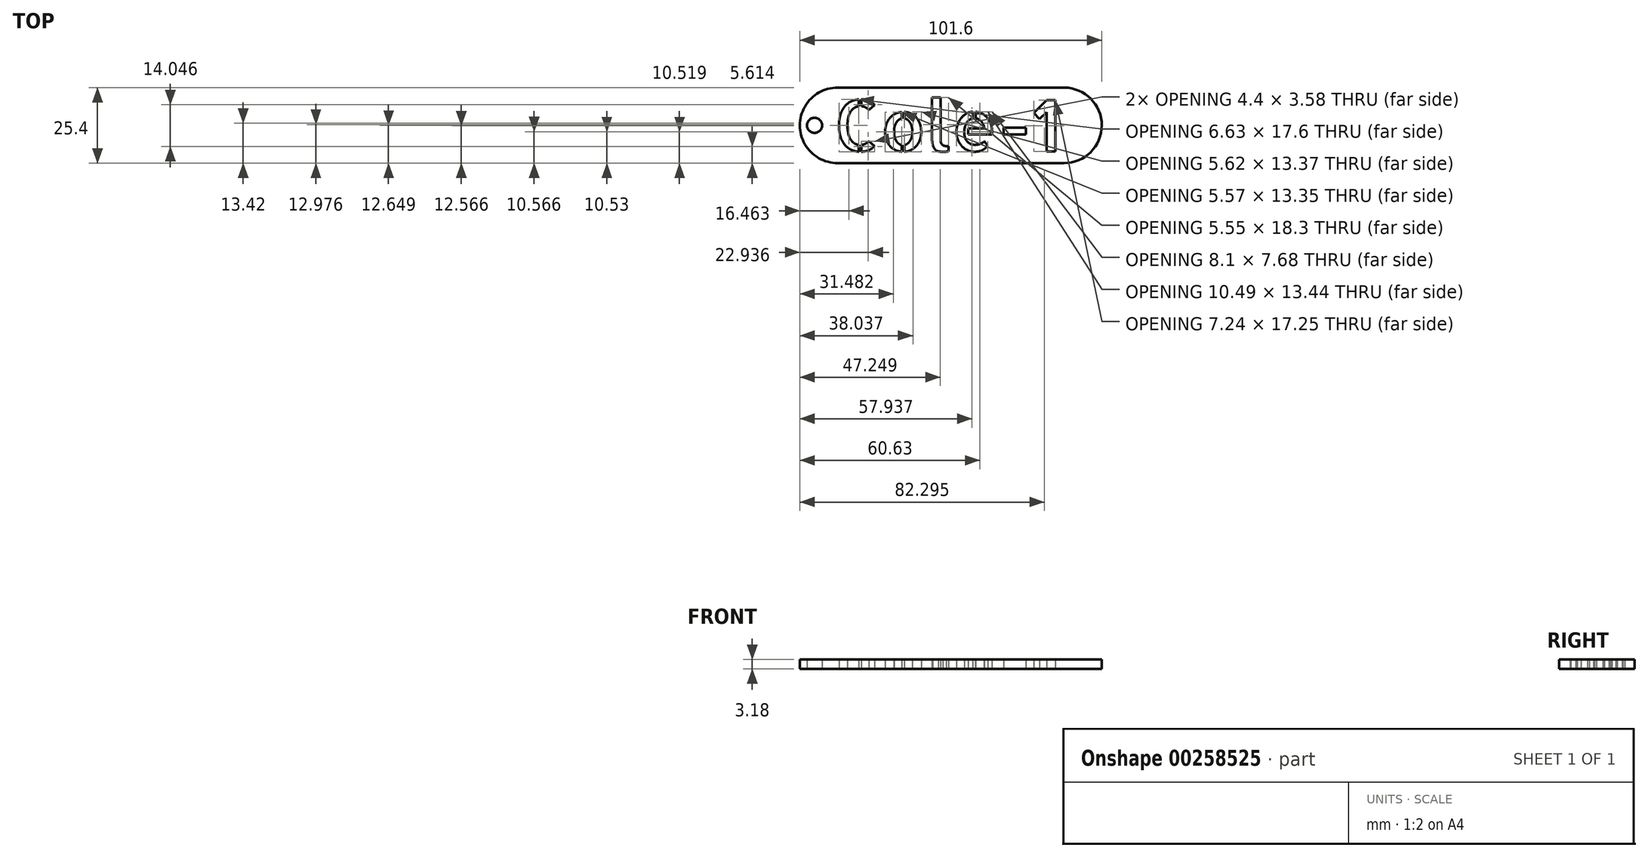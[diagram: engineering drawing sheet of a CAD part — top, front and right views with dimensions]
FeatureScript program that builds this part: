
annotation { "Feature Type Name" : "Feature", "Feature Type Description" : "" }
export const myFeature = defineFeature(function(context is Context, id is Id, definition is map)
    precondition{}
    {
        {
            var Q0;
            Q0=qCreatedBy(makeId("Top.planeOp"),FACE);
            var sketch = newSketch(context, id + "F0", { "sketchPlane" : qUnion([Q0])});
            skArc(sketch, "E0", {"start": v(38.06, -12.7) * mm, "mid": v(50.8, 0.02) * mm, "end": v(38.02, 12.7) * mm});
            skArc(sketch, "E1", {"start": v(-38.02, 12.7) * mm, "mid": v(-50.8, 0.02) * mm, "end": v(-38.06, -12.7) * mm});
            skLineSegment(sketch, "E2", {"start": v(-38.02, 12.7) * mm, "end": v(38.18, 12.7) * mm});
            skLineSegment(sketch, "E3", {"start": v(-38.06, -12.7) * mm, "end": v(38.14, -12.7) * mm});
            skPoint(sketch, "E4.orphan", {"position": v(0, 0) * mm});
            skCircle(sketch, "E5", {"center": v(-45.85, 0) * mm, "radius": 2.54 * mm});
            skText(sketch, "E6", { "text": "Cole-1", "fontName": "AllertaStencil-Regular.ttf"});
            const initialGuessF0  = {"E6": [-0.0395, -0.00876, 1, 0, 0.01726]};
            skSetInitialGuess(sketch, initialGuessF0);
            skSolve(sketch);
        }
        {
            var Q0;
            {var subQ5=sQuery(id+"F0.wireOp",EDGE,"E1");Q0=makeQuery(id+"F0.imprint","IMPRINT",FACE,{"disambiguationData":[TD([[makeQuery(id+"F0.imprint","IMPRINT",EDGE,{"derivedFrom":subQ5}),1.0]])]});}
            extrude(context, id + "F1", {"entities" : qUnion([Q0]), "depth" : 3.17 * mm});
        }
    });
